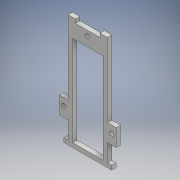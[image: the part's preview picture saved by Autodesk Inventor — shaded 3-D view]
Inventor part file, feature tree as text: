
AUTODESK INVENTOR PART (.ipt)
format: ipt  version: 2017 (Build 210142000, 142)  size: 162,816 bytes
history: native  units: mm
features: other x3, extrude x2, sketch x2, projected_geometry x1
ambient origin geometry x8: Origin, YZ Plane, XZ Plane, XY Plane, X Axis, Y Axis, Z Axis, Center Point
bodies: Solid1 (feature_tree)
feature tree (8):
  other  "k2_t_l4.ipt"
  extrude  "Extrusion1"  Depth=3.0mm
  extrude  "Extrusion2"  Depth=10.0mm TaperAngle=0.0deg
  other  "Solid1::k2_t_l4.ipt"
  other  "TaggingFeature1"
  sketch  "Sketch1"  dims[d0=10.0mm]
  projected_geometry  "Projected Loop1"
  sketch  "Sketch2"  dims[d2=3.0mm d3=0.0mm d8=3.0mm d9=3.0mm d11=33.0mm d12=12.0mm d13=60.415173mm d14=12.0mm d6=3.0mm d10=10.0mm d15=0.0mm d16=3.0mm d18=2.517299mm d19=0.0mm d21=21.0mm d22=10.0mm]
